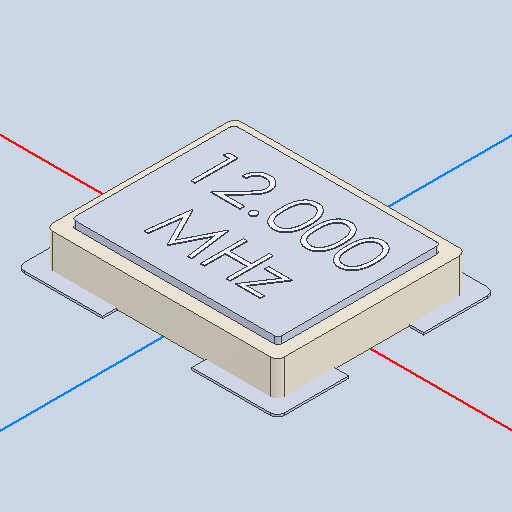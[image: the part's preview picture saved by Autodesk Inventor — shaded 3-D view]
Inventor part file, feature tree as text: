
AUTODESK INVENTOR PART (.ipt)
format: ipt  version: 2022 (Build 260153000, 153)  size: 300,544 bytes
history: native  units: mm
features: other x11, fillet x1
ambient origin geometry x8: Origin, YZ Plane, XZ Plane, XY Plane, X Axis, Y Axis, Z Axis, Center Point
bodies: Body1 (feature_tree), Body2 (feature_tree), Body3 (feature_tree), Body4 (feature_tree), Body5 (feature_tree), Body6 (feature_tree)
feature tree (12):
  other  "Твердое тело1"
  other  "Твердое тело2"
  other  "Твердое тело3"
  other  "Твердое тело4"
  other  "Твердое тело5"
  other  "Твердое тело6"
  fillet  "Fillet1"  [1 undecoded]
  other  "Boss-Extrude3[1]"
  other  "Boss-Extrude3[2]"
  other  "Boss-Extrude3[3]"
  other  "Boss-Extrude3[4]"
  other  "Boss-Extrude4"
note: 1 required parameter value undecoded (feature->parameter linkage not recoverable at this tier; creation-order binding heuristic only, values carry confidence <= 0.55)
